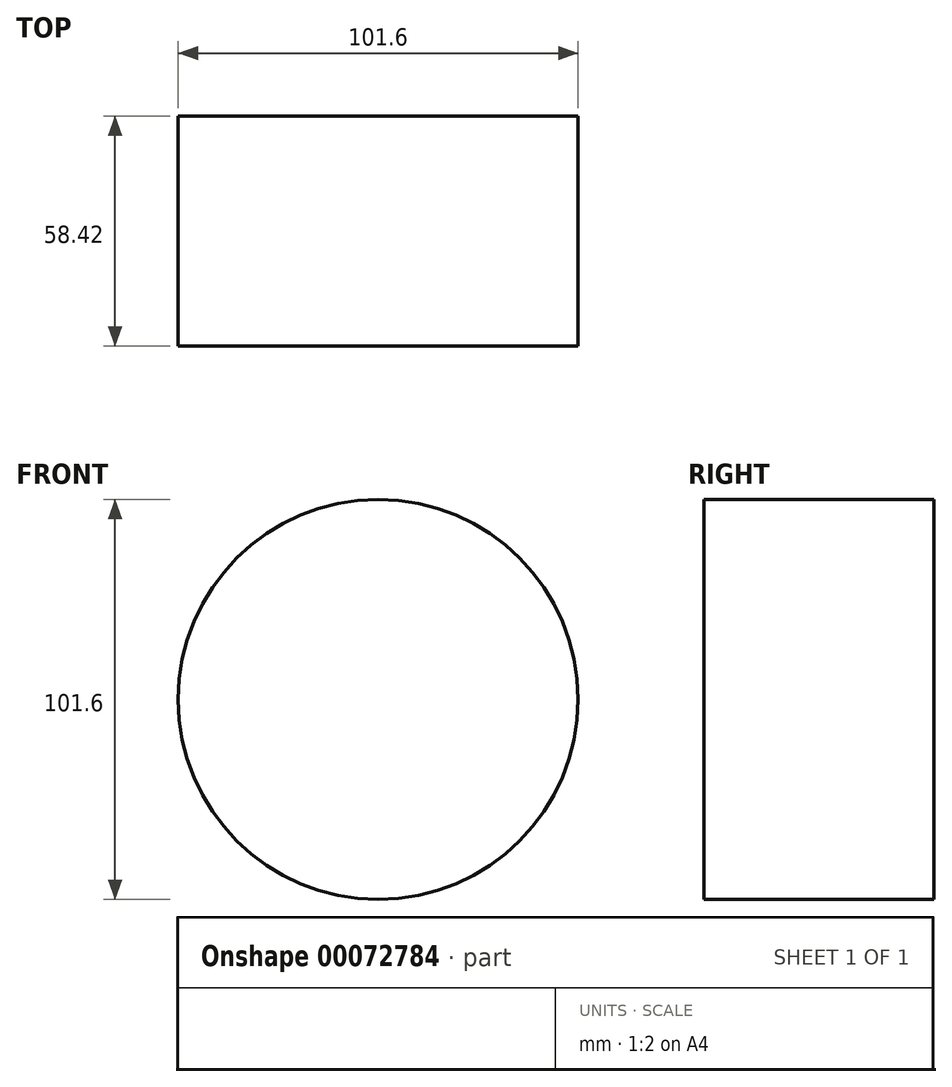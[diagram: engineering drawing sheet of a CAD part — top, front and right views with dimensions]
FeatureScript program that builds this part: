
annotation { "Feature Type Name" : "Feature", "Feature Type Description" : "" }
export const myFeature = defineFeature(function(context is Context, id is Id, definition is map)
    precondition{}
    {
        {
            var Q0;
            Q0=qCreatedBy(makeId("Front.planeOp"),FACE);
            var sketch = newSketch(context, id + "F0", { "sketchPlane" : qUnion([Q0])});
            skCircle(sketch, "E0", {"center": v(0, 0) * mm, "radius": 50.8 * mm});
            skSolve(sketch);
        }
        {
            var Q0;
            Q0=makeQuery(id+"F0.imprint","IMPRINT",FACE,{"disambiguationData":[TD([[makeQuery(id+"F0.imprint","IMPRINT",EDGE,{"derivedFrom":sQuery(id+"F0.wireOp",EDGE,"E0")}),1.0]])]});
            extrude(context, id + "F1", {"entities" : qUnion([Q0]), "endBound" : BoundingType.SYMMETRIC, "depth" : 58.42 * mm});
        }
    });
